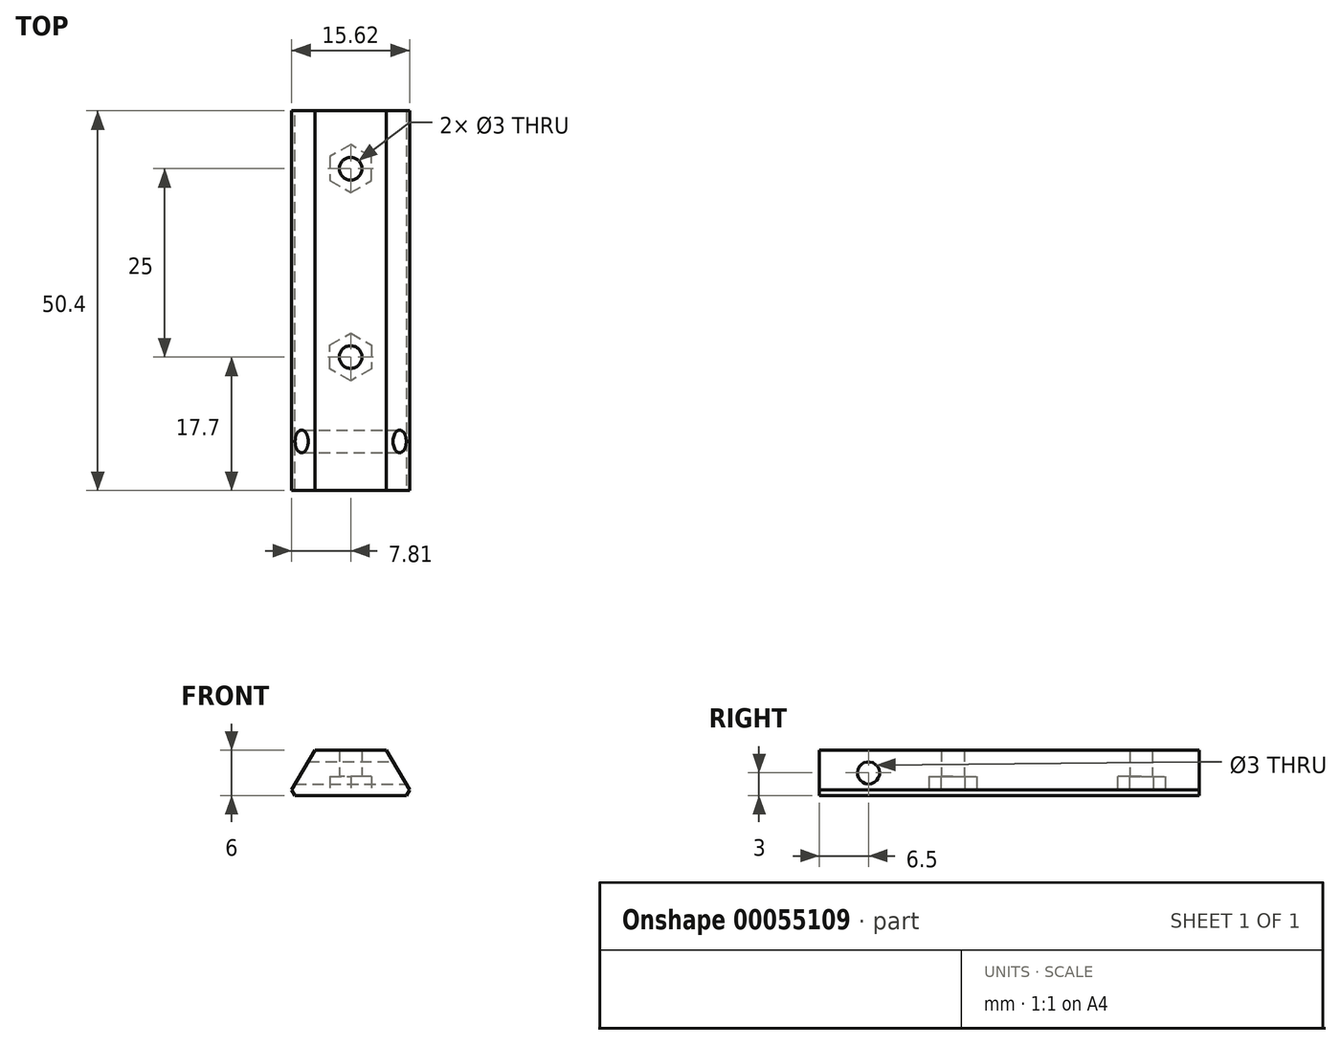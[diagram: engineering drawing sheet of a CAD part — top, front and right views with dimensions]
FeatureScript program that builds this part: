
annotation { "Feature Type Name" : "Feature", "Feature Type Description" : "" }
export const myFeature = defineFeature(function(context is Context, id is Id, definition is map)
    precondition{}
    {
        {
            var Q0;
            Q0=qCreatedBy(makeId("Front.planeOp"),FACE);
            var sketch = newSketch(context, id + "F0", { "sketchPlane" : qUnion([Q0])});
            skLineSegment(sketch, "E0.rect.top", {"start": v(4.75, 6) * mm, "end": v(-4.75, 6) * mm});
            skPoint(sketch, "E0.rect.middle", {"position": v(0, 0) * mm});
            skPoint(sketch, "E1.rect.middle", {"position": v(0, 6) * mm});
            skLineSegment(sketch, "E2", {"start": v(4.75, 6) * mm, "end": v(8.25, 0) * mm});
            skLineSegment(sketch, "E3", {"start": v(-4.75, 6) * mm, "end": v(-8.25, 0) * mm});
            skLineSegment(sketch, "E4", {"start": v(-8.25, 0) * mm, "end": v(8.25, 0) * mm});
            skPoint(sketch, "E5.orphan", {"position": v(-4.75, 7.55) * mm});
            skPoint(sketch, "E6.orphan", {"position": v(-8.25, 6) * mm});
            skPoint(sketch, "E0.rect.bottom.end.orphan", {"position": v(-8.25, -6) * mm});
            skPoint(sketch, "E7.orphan", {"position": v(8.25, -6) * mm});
            skPoint(sketch, "E8.orphan", {"position": v(8.25, 6) * mm});
            skPoint(sketch, "E1.rect.left.start.orphan", {"position": v(4.75, 4.45) * mm});
            skPoint(sketch, "E1.rect.right.start.orphan", {"position": v(-4.75, 4.45) * mm});
            skSolve(sketch);
        }
        {
            var Q0;
            Q0 = qSketchRegion(id + "F0", true);
            extrude(context, id + "F1", {"entities" : qUnion([Q0]), "depth" : 50.4 * mm});
        }
        {
            var Q0;
            Q0=qCreatedBy(makeId("Top.planeOp"),FACE);
            var sketch = newSketch(context, id + "F2", { "sketchPlane" : qUnion([Q0])});
            skLineSegment(sketch, "E9", {"start": v(0, 0) * mm, "end": v(0, -20.2) * mm});
            skLineSegment(sketch, "E10", {"start": v(0, -20.2) * mm, "end": v(0, -32.7) * mm});
            skCircle(sketch, "E11", {"center": v(0, -32.7) * mm, "radius": 1.5 * mm});
            skCircle(sketch, "E12.cCircle", {"center": v(0, -32.7) * mm, "radius": 2.75 * mm, "construction": true});
            skLineSegment(sketch, "E12.0", {"start": v(2.75, -31.11) * mm, "end": v(2.75, -34.29) * mm});
            skLineSegment(sketch, "E12.1", {"start": v(2.75, -34.29) * mm, "end": v(0, -35.88) * mm});
            skLineSegment(sketch, "E12.2", {"start": v(0, -35.88) * mm, "end": v(-2.75, -34.29) * mm});
            skLineSegment(sketch, "E12.3", {"start": v(-2.75, -34.29) * mm, "end": v(-2.75, -31.11) * mm});
            skLineSegment(sketch, "E12.4", {"start": v(-2.75, -31.11) * mm, "end": v(0, -29.52) * mm});
            skLineSegment(sketch, "E12.5", {"start": v(0, -29.52) * mm, "end": v(2.75, -31.11) * mm});
            skPoint(sketch, "E12.0.midPoint", {"position": v(2.75, -32.7) * mm});
            skLineSegment(sketch, "E13", {"start": v(0, -20.2) * mm, "end": v(-2.31, -20.2) * mm});
            skLineSegment(sketch, "E14.MirrorCS", {"start": v(2.75, -6.11) * mm, "end": v(0, -4.52) * mm});
            skLineSegment(sketch, "E15.MirrorCS", {"start": v(2.75, -9.29) * mm, "end": v(2.75, -6.11) * mm});
            skLineSegment(sketch, "E16.MirrorCS", {"start": v(0, -4.52) * mm, "end": v(-2.75, -6.11) * mm});
            skLineSegment(sketch, "E17.MirrorCS", {"start": v(-2.75, -6.11) * mm, "end": v(-2.75, -9.29) * mm});
            skLineSegment(sketch, "E18.MirrorCS", {"start": v(0, -10.88) * mm, "end": v(2.75, -9.29) * mm});
            skLineSegment(sketch, "E19.MirrorCS", {"start": v(-2.75, -9.29) * mm, "end": v(0, -10.88) * mm});
            skPoint(sketch, "E20.MirrorP", {"position": v(2.75, -7.7) * mm});
            skCircle(sketch, "E21.MirrorC", {"center": v(0, -7.7) * mm, "radius": 1.5 * mm});
            skCircle(sketch, "E22.MirrorC", {"center": v(0, -7.7) * mm, "radius": 2.75 * mm, "construction": true});
            skSolve(sketch);
        }
        {
            var Q0;
            Q0=makeQuery(id+"F2.imprint","IMPRINT",FACE,{"disambiguationData":[TD([[makeQuery(id+"F2.imprint","IMPRINT",EDGE,{"derivedFrom":sQuery(id+"F2.wireOp",EDGE,"E11")}),1.0]])]});
            var Q1;
            {var subQ0=sQuery(id+"F2.wireOp",EDGE,"E21.MirrorC");var subQ1=sQuery(id+"F2.wireOp",EDGE,"E9");var subQ2=makeQuery(id+"F2.imprint","INTERSECT",VERTEX,{"disambiguationData":[OD(0.0)],"derivedFrom":[subQ1,subQ0]});Q1=makeQuery(id+"F2.imprint","IMPRINT",FACE,{"disambiguationData":[TD([[makeQuery(id+"F2.imprint","IMPRINT",EDGE,{"disambiguationData":[TD([[subQ2,-1.0]])],"derivedFrom":subQ1}),-1.0]])]});}
            var Q2;
            {var subQ0=sQuery(id+"F2.wireOp",EDGE,"E21.MirrorC");var subQ1=sQuery(id+"F2.wireOp",EDGE,"E9");var subQ2=makeQuery(id+"F2.imprint","INTERSECT",VERTEX,{"disambiguationData":[OD(0.0)],"derivedFrom":[subQ1,subQ0]});Q2=makeQuery(id+"F2.imprint","IMPRINT",FACE,{"disambiguationData":[TD([[makeQuery(id+"F2.imprint","IMPRINT",EDGE,{"disambiguationData":[TD([[subQ2,-1.0]])],"derivedFrom":subQ1}),1.0]])]});}
            extrude(context, id + "F3", {"entities" : qUnion([Q0, Q1, Q2]), "operationType" : NewBodyOperationType.REMOVE, "endBound" : BoundingType.THROUGH_ALL, "depth" : 25 * mm});
        }
        {
            var Q0;
            Q0 = qSketchRegion(id + "F2", true);
            extrude(context, id + "F4", {"entities" : qUnion([Q0]), "operationType" : NewBodyOperationType.REMOVE, "depth" : 2.5 * mm});
        }
        {
            var Q0;
            Q0=qCreatedBy(makeId("Right.planeOp"),FACE);
            var sketch = newSketch(context, id + "F5", { "sketchPlane" : qUnion([Q0])});
            skLineSegment(sketch, "E23", {"start": v(0, 0) * mm, "end": v(-43.9, 0) * mm});
            skLineSegment(sketch, "E24", {"start": v(-43.9, 0) * mm, "end": v(-43.9, 6) * mm});
            skCircle(sketch, "E25", {"center": v(-43.9, 3) * mm, "radius": 1.5 * mm});
            skSolve(sketch);
        }
        {
            var Q0;
            Q0 = qSketchRegion(id + "F5", true);
            extrude(context, id + "F6", {"entities" : qUnion([Q0]), "operationType" : NewBodyOperationType.REMOVE, "endBound" : BoundingType.THROUGH_ALL, "oppositeDirection" : true, "depth" : 25 * mm, "hasSecondDirection" : true, "secondDirectionBound" : SecondDirectionBoundingType.THROUGH_ALL, "secondDirectionOppositeDirection" : false, "secondDirectionDepth" : 25 * mm});
        }
        {
            var Q0;
            Q0=makeQuery(id+"F1.opExtrude","SWEPT_EDGE",EDGE,{"disambiguationData":[OSD([sQuery(id+"F0.wireOp",EDGE,"E3"),sQuery(id+"F0.wireOp",EDGE,"E4")])]});
            var Q1;
            Q1=makeQuery(id+"F1.opExtrude","SWEPT_EDGE",EDGE,{"disambiguationData":[OSD([sQuery(id+"F0.wireOp",EDGE,"E2"),sQuery(id+"F0.wireOp",EDGE,"E4")])]});
            chamfer(context, id + "F7", {"entities" : qUnion([Q0, Q1]), "width" : 0.5 * mm, "tangentPropagation" : true});
        }
    });
